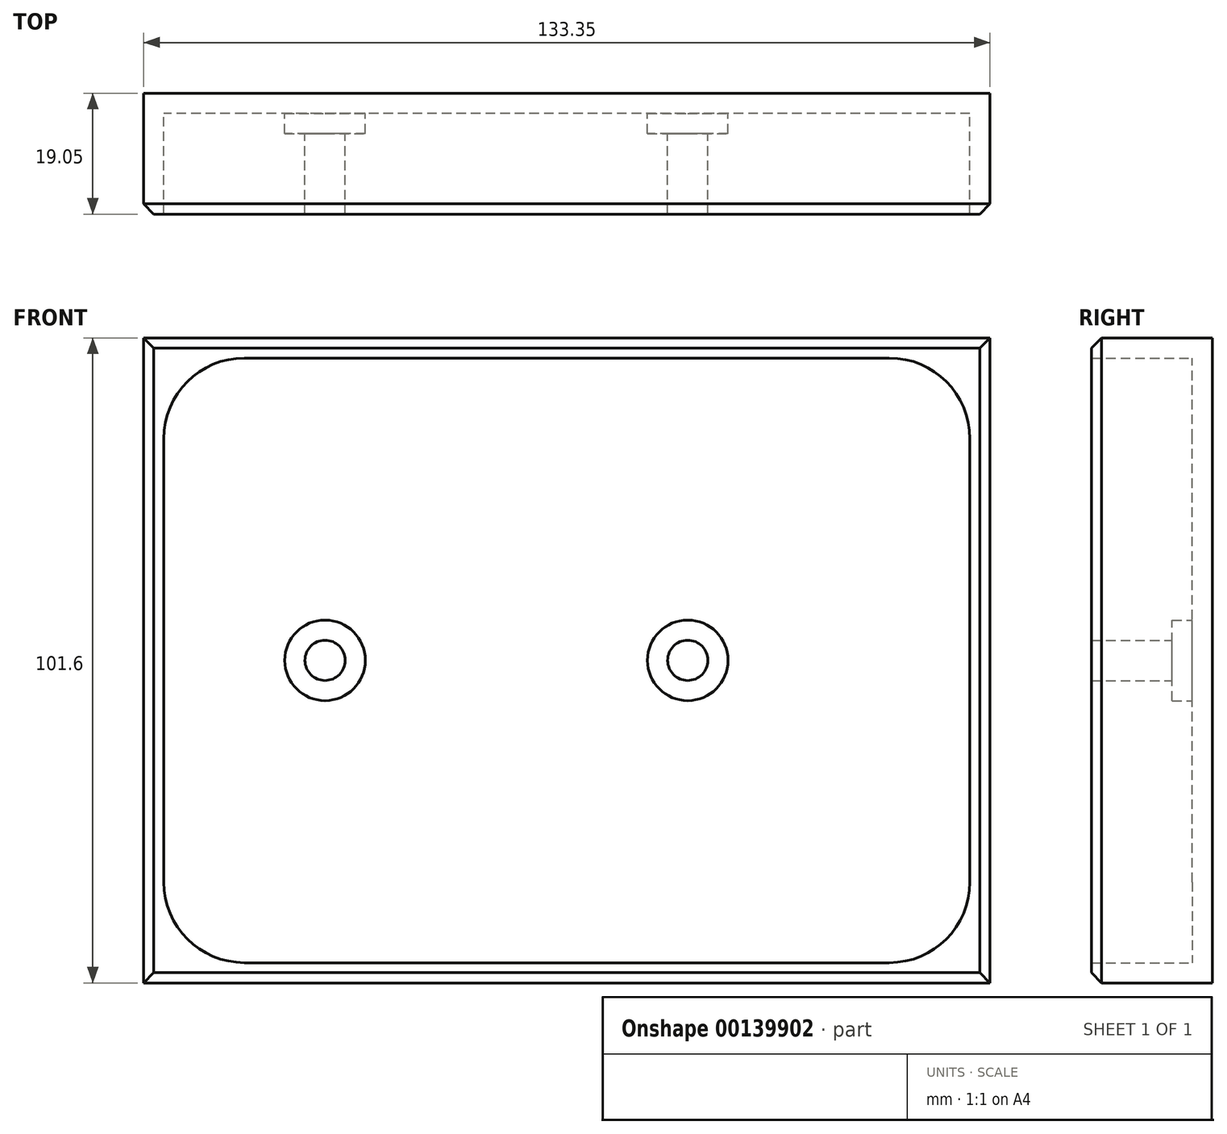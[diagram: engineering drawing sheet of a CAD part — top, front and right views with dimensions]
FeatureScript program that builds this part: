
annotation { "Feature Type Name" : "Feature", "Feature Type Description" : "" }
export const myFeature = defineFeature(function(context is Context, id is Id, definition is map)
    precondition{}
    {
        {
            var Q0;
            Q0=qCreatedBy(makeId("Front.planeOp"),FACE);
            var sketch = newSketch(context, id + "F0", { "sketchPlane" : qUnion([Q0])});
            skLineSegment(sketch, "E0.bottom", {"start": v(61.56, -44.1) * mm, "end": v(-71.79, -44.1) * mm});
            skLineSegment(sketch, "E0.top", {"start": v(61.56, 57.5) * mm, "end": v(-71.79, 57.5) * mm});
            skLineSegment(sketch, "E0.left", {"start": v(61.56, -44.1) * mm, "end": v(61.56, 57.5) * mm});
            skLineSegment(sketch, "E0.right", {"start": v(-71.79, -44.1) * mm, "end": v(-71.79, 57.5) * mm});
            skSolve(sketch);
        }
        {
            var Q0;
            Q0=makeQuery(id+"F0.imprint","IMPRINT",FACE,{"disambiguationData":[TD([[makeQuery(id+"F0.imprint","IMPRINT",EDGE,{"derivedFrom":sQuery(id+"F0.wireOp",EDGE,"E0.bottom")}),-1.0]])]});
            extrude(context, id + "F1", {"entities" : qUnion([Q0]), "depth" : 19.05 * mm});
        }
        {
            var Q0;
            Q0=makeQuery(id+"F1.opExtrude","CAP_FACE",FACE,{"disambiguationData":[OSD([sQuery(id+"F0.wireOp",EDGE,"E0.bottom"),sQuery(id+"F0.wireOp",EDGE,"E0.top"),sQuery(id+"F0.wireOp",EDGE,"E0.left"),sQuery(id+"F0.wireOp",EDGE,"E0.right")])],"isStart":false});
            shell(context, id + "F2", {"entities" : qUnion([Q0]), "thickness" : 3.17 * mm});
        }
        {
            var Q0;
            Q0=makeQuery(id+"F2.opShell","OFFSET_FACE",FACE,{"disambiguationData":[OSD([sQuery(id+"F0.wireOp",EDGE,"E0.bottom"),sQuery(id+"F0.wireOp",EDGE,"E0.top"),sQuery(id+"F0.wireOp",EDGE,"E0.left"),sQuery(id+"F0.wireOp",EDGE,"E0.right")])]});
            var sketch = newSketch(context, id + "F3", { "sketchPlane" : qUnion([Q0])});
            skCircle(sketch, "E1", {"center": v(-43.21, 6.7) * mm, "radius": 6.35 * mm});
            skPoint(sketch, "E1.centerSnap0", {"position": v(-68.61, 6.7) * mm});
            skCircle(sketch, "E2", {"center": v(13.94, 6.7) * mm, "radius": 6.35 * mm});
            skSolve(sketch);
        }
        {
            var Q0;
            Q0 = qSketchRegion(id + "F3", true);
            extrude(context, id + "F4", {"entities" : qUnion([Q0]), "operationType" : NewBodyOperationType.ADD, "depth" : 3.17 * mm});
        }
        {
            var Q0;
            Q0=makeQuery(id+"F4.opExtrude","CAP_FACE",FACE,{"disambiguationData":[OSD([sQuery(id+"F3.wireOp",EDGE,"E1")])],"isStart":false});
            var sketch = newSketch(context, id + "F5", { "sketchPlane" : qUnion([Q0])});
            skCircle(sketch, "E3", {"center": v(-43.21, 6.7) * mm, "radius": 3.18 * mm});
            skSolve(sketch);
        }
        {
            var Q0;
            Q0 = qSketchRegion(id + "F5", true);
            extrude(context, id + "F6", {"entities" : qUnion([Q0]), "operationType" : NewBodyOperationType.ADD, "depth" : 12.7 * mm});
        }
        {
            var Q0;
            Q0=makeQuery(id+"F4.opExtrude","CAP_FACE",FACE,{"disambiguationData":[OSD([sQuery(id+"F3.wireOp",EDGE,"E2")])],"isStart":false});
            var sketch = newSketch(context, id + "F7", { "sketchPlane" : qUnion([Q0])});
            skCircle(sketch, "E4", {"center": v(13.94, 6.7) * mm, "radius": 3.18 * mm});
            skSolve(sketch);
        }
        {
            var Q0;
            Q0 = qSketchRegion(id + "F7", true);
            extrude(context, id + "F8", {"entities" : qUnion([Q0]), "operationType" : NewBodyOperationType.ADD, "depth" : 12.7 * mm});
        }
        {
            var Q0;
            Q0=makeQuery(id+"F2.opShell","OFFSET_EDGE",EDGE,{"disambiguationData":[OSD([sQuery(id+"F0.wireOp",EDGE,"E0.bottom"),sQuery(id+"F0.wireOp",EDGE,"E0.right")])]});
            var Q1;
            Q1=makeQuery(id+"F2.opShell","OFFSET_EDGE",EDGE,{"disambiguationData":[OSD([sQuery(id+"F0.wireOp",EDGE,"E0.bottom"),sQuery(id+"F0.wireOp",EDGE,"E0.left")])]});
            var Q2;
            Q2=makeQuery(id+"F2.opShell","OFFSET_EDGE",EDGE,{"disambiguationData":[OSD([sQuery(id+"F0.wireOp",EDGE,"E0.top"),sQuery(id+"F0.wireOp",EDGE,"E0.right")])]});
            var Q3;
            Q3=makeQuery(id+"F2.opShell","OFFSET_EDGE",EDGE,{"disambiguationData":[OSD([sQuery(id+"F0.wireOp",EDGE,"E0.top"),sQuery(id+"F0.wireOp",EDGE,"E0.left")])]});
            fillet(context, id + "F9", {"entities" : qUnion([Q0, Q1, Q2, Q3]), "radius" : 12.7 * mm, "tangentPropagation" : true, "allowEdgeOverflow" : false});
        }
        {
            var Q0;
            Q0=makeQuery(id+"F1.opExtrude","CAP_EDGE",EDGE,{"disambiguationData":[OSD([sQuery(id+"F0.wireOp",EDGE,"E0.left")])],"isStart":false});
            var Q1;
            Q1=makeQuery(id+"F1.opExtrude","CAP_EDGE",EDGE,{"disambiguationData":[OSD([sQuery(id+"F0.wireOp",EDGE,"E0.bottom")])],"isStart":false});
            var Q2;
            Q2=makeQuery(id+"F1.opExtrude","CAP_EDGE",EDGE,{"disambiguationData":[OSD([sQuery(id+"F0.wireOp",EDGE,"E0.right")])],"isStart":false});
            var Q3;
            Q3=makeQuery(id+"F1.opExtrude","CAP_EDGE",EDGE,{"disambiguationData":[OSD([sQuery(id+"F0.wireOp",EDGE,"E0.top")])],"isStart":false});
            chamfer(context, id + "F10", {"entities" : qUnion([Q0, Q1, Q2, Q3]), "width" : 1.6 * mm, "tangentPropagation" : true});
        }
    });
